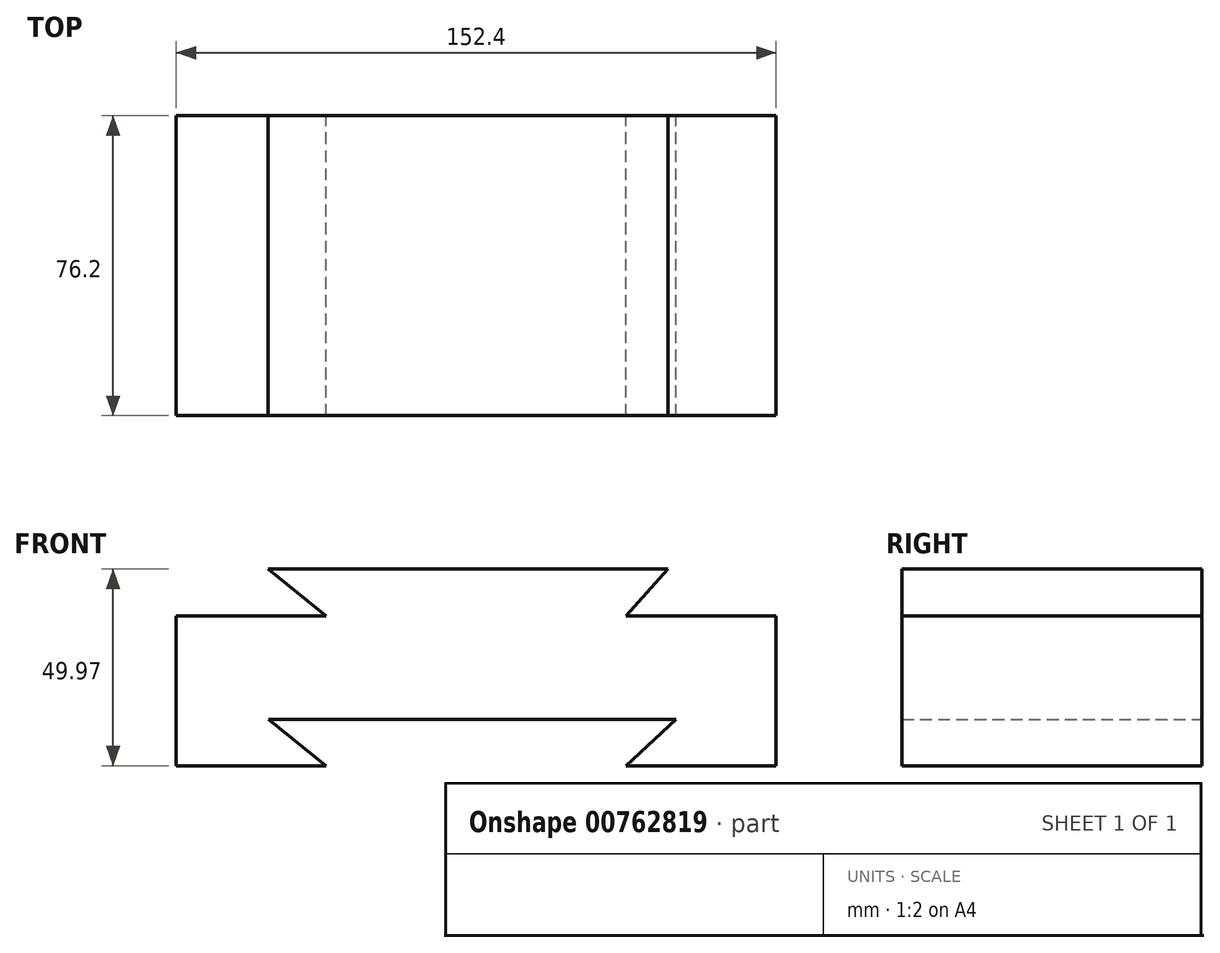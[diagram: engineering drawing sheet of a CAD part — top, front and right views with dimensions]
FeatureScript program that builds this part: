
annotation { "Feature Type Name" : "Feature", "Feature Type Description" : "" }
export const myFeature = defineFeature(function(context is Context, id is Id, definition is map)
    precondition{}
    {
        {
            var Q0;
            Q0=qCreatedBy(makeId("Front.planeOp"),FACE);
            var sketch = newSketch(context, id + "F0", { "sketchPlane" : qUnion([Q0])});
            skLineSegment(sketch, "E0", {"start": v(26.8, -53.87) * mm, "end": v(64.9, -53.87) * mm});
            skLineSegment(sketch, "E1", {"start": v(64.9, -53.87) * mm, "end": v(64.9, -15.77) * mm});
            skLineSegment(sketch, "E2", {"start": v(64.9, -15.77) * mm, "end": v(26.8, -15.77) * mm});
            skLineSegment(sketch, "E3", {"start": v(26.8, -15.77) * mm, "end": v(37.45, -3.9) * mm});
            skLineSegment(sketch, "E4", {"start": v(37.45, -3.9) * mm, "end": v(-64.15, -3.9) * mm});
            skLineSegment(sketch, "E5", {"start": v(-64.15, -3.9) * mm, "end": v(-49.4, -15.77) * mm});
            skLineSegment(sketch, "E6", {"start": v(-49.4, -15.77) * mm, "end": v(-87.5, -15.77) * mm});
            skLineSegment(sketch, "E7", {"start": v(-87.5, -53.87) * mm, "end": v(-49.4, -53.87) * mm});
            skLineSegment(sketch, "E8", {"start": v(-49.4, -53.87) * mm, "end": v(-64, -42.12) * mm});
            skLineSegment(sketch, "E9", {"start": v(-64, -42.12) * mm, "end": v(39.5, -42.12) * mm});
            skLineSegment(sketch, "E10", {"start": v(39.5, -42.12) * mm, "end": v(26.8, -53.87) * mm});
            skLineSegment(sketch, "E11", {"start": v(-87.5, -15.77) * mm, "end": v(-87.5, -53.87) * mm});
            skSolve(sketch);
        }
        {
            var Q0;
            Q0 = qSketchRegion(id + "F0", true);
            extrude(context, id + "F1", {"entities" : qUnion([Q0]), "depth" : 76.2 * mm, "offsetDistance" : 25.4 * mm});
        }
    });
